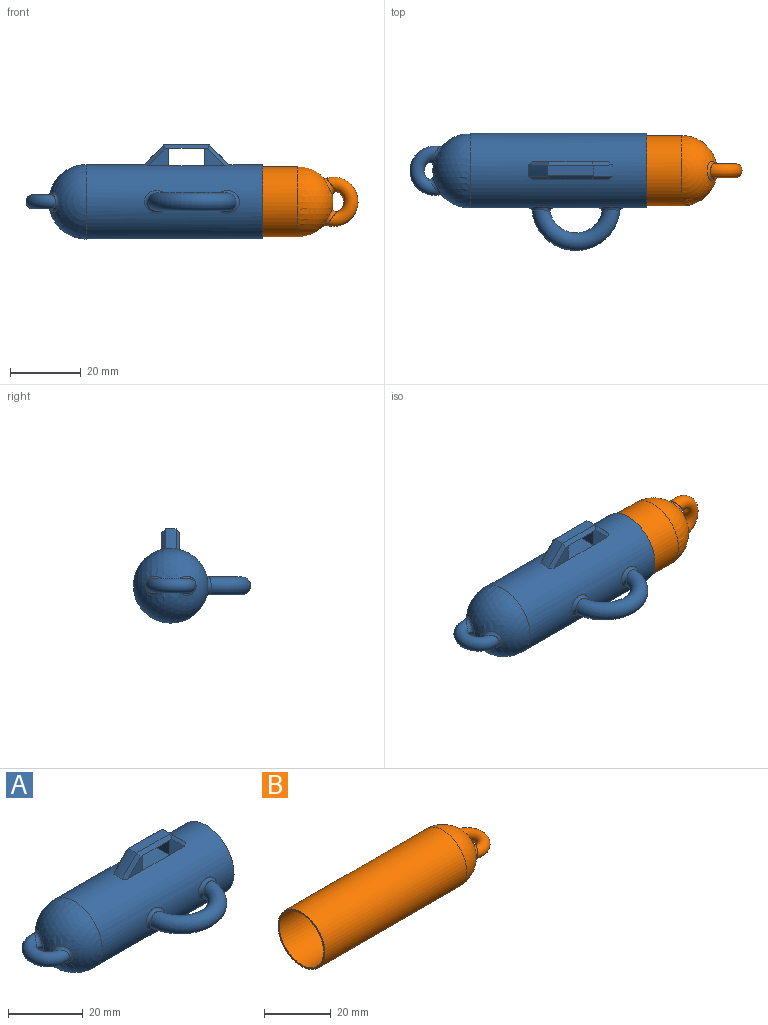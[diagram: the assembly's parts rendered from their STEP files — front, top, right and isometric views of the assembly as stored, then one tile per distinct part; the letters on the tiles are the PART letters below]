
ASSEMBLY  parts=2 mates=1
PART A: 32 faces, bbox 69.2x35.8x28.3 mm
  f0: plane 5.78x4.86mm, normal (0,1,0), area 16.3mm2, adj f2,f19,f26,f27
  f1: plane 5.78x4.86mm, normal (0,-1,0), area 16.3mm2, adj f2,f16,f22,f23
  f2: cylinder r=10.55mm len=50mm, axis (-1,0,0), area 3123.4mm2, adj f0,f1,f4,f6,f13,f14,f17,f20
  f3: cylinder r=10.05mm len=50mm, axis (-1,0,0), area 3157.3mm2, adj f4,f5
  f4: plane 21.1x21.1mm, normal (1,0,0), area 32.4mm2, adj f2,f3
  f5: sphere r=10.05mm, area 617.7mm2, adj f3,f9,f10,f11,f12
  f6: sphere r=10.55mm, area 643.2mm2, adj f2,f28,f29
  f7: torus R=10mm, axis (0,0,-1), area 455.5mm2, adj f30,f31
  f8: torus R=5mm, axis (0,0,1), area 188.7mm2, adj f28,f29
  f9: plane 5.34x4.52mm, normal (0.95,0.31,0), area 10.7mm2, adj f5,f10
  f10: torus R=5mm, axis (0,0,1), area 2.6mm2, adj f5,f9
  f11: plane 5.62x4.51mm, normal (0.96,-0.29,0), area 9.4mm2, adj f5,f12
  f12: torus R=5mm, axis (0,0,1), area 2.1mm2, adj f5,f11
  f13: plane 5.78x4.86mm, normal (0,-1,0), area 16.3mm2, adj f2,f19,f23,f24
  f14: plane 5.78x4.86mm, normal (0,1,0), area 16.3mm2, adj f2,f16,f25,f26
  f15: plane 12.9x3mm, normal (0,0,1), area 38.6mm2, adj f20,f21,f23,f26
  f16: plane 5x4.85mm, normal (-1,0,0), area 24.3mm2, adj f1,f14,f17,f18
  f17: plane 10x5mm, normal (0,0,1), area 50mm2, adj f2,f16,f19
  f18: plane 10x5mm, normal (0,0,-1), area 50mm2, adj f16,f19,f23,f26
  f19: plane 5x4.85mm, normal (1,0,0), area 24.3mm2, adj f0,f13,f17,f18
  f20: cone r=16.55mm half-angle=45deg, axis (1,0,0), area 25.1mm2, adj f2,f15,f23,f24,f26,f27
  f21: cone r=10.55mm half-angle=45deg, axis (-1,0,0), area 25.1mm2, adj f2,f15,f22,f23,f25,f26
  f22: bspline ~6.3x6.27mm, area 10mm2, adj f1,f2,f21,f23
  f23: plane 12.89x1mm, normal (0,-0.71,0.71), area 17.6mm2, adj f1,f13,f15,f18,f20,f21,f22,f24
  f24: bspline ~6.3x6.27mm, area 10mm2, adj f2,f13,f20,f23
  f25: bspline ~6.3x6.27mm, area 10mm2, adj f2,f14,f21,f26
  f26: plane 12.89x1mm, normal (0,0.71,0.71), area 17.6mm2, adj f0,f14,f15,f18,f20,f21,f25,f27
  f27: bspline ~6.3x6.27mm, area 10mm2, adj f0,f2,f20,f26
  f28: bspline ~5.94x5.49mm, area 23.6mm2, adj f6,f8
  f29: bspline ~5.94x5.49mm, area 23.6mm2, adj f6,f8
  f30: bspline ~7.09x6.4mm, area 25.6mm2, adj f2,f7
  f31: bspline ~7.1x6.4mm, area 25.7mm2, adj f2,f7
PART B: 12 faces, bbox 77.6x19.9x19.9 mm
  f0: sphere r=9.35mm, area 539.1mm2, adj f2,f6,f7,f8,f9
  f1: sphere r=9.95mm, area 570.2mm2, adj f3,f10,f11
  f2: cylinder r=9.35mm len=60mm, axis (-1,0,0), area 3524.9mm2, adj f0,f4
  f3: cylinder r=9.95mm len=60mm, axis (-1,0,0), area 3751.1mm2, adj f1,f4
  f4: plane 19.9x19.9mm, normal (-1,0,0), area 36.4mm2, adj f2,f3
  f5: torus R=5mm, axis (0,0,1), area 211.4mm2, adj f10,f11
  f6: torus R=5mm, axis (0,0,1), area 0.3mm2, adj f0,f7
  f7: plane 3.28x2.35mm, normal (-0.92,-0.39,0), area 6.4mm2, adj f0,f6
  f8: plane 2.41x1.81mm, normal (-0.93,0.37,0), area 3.8mm2, adj f0,f9
  f9: torus R=5mm, axis (0,0,1), area 0.1mm2, adj f0,f8
  f10: bspline ~5.46x5.33mm, area 21.2mm2, adj f1,f5
  f11: bspline ~5.46x5.32mm, area 21.2mm2, adj f1,f5
PLACE A at identity fixed
PLACE B rot(axis=(1,0,0),90deg) t=(0,0,0)mm
MATE slider A.f3 <-> B.f2  axis (-1,0,0) through (50,0,0)mm
